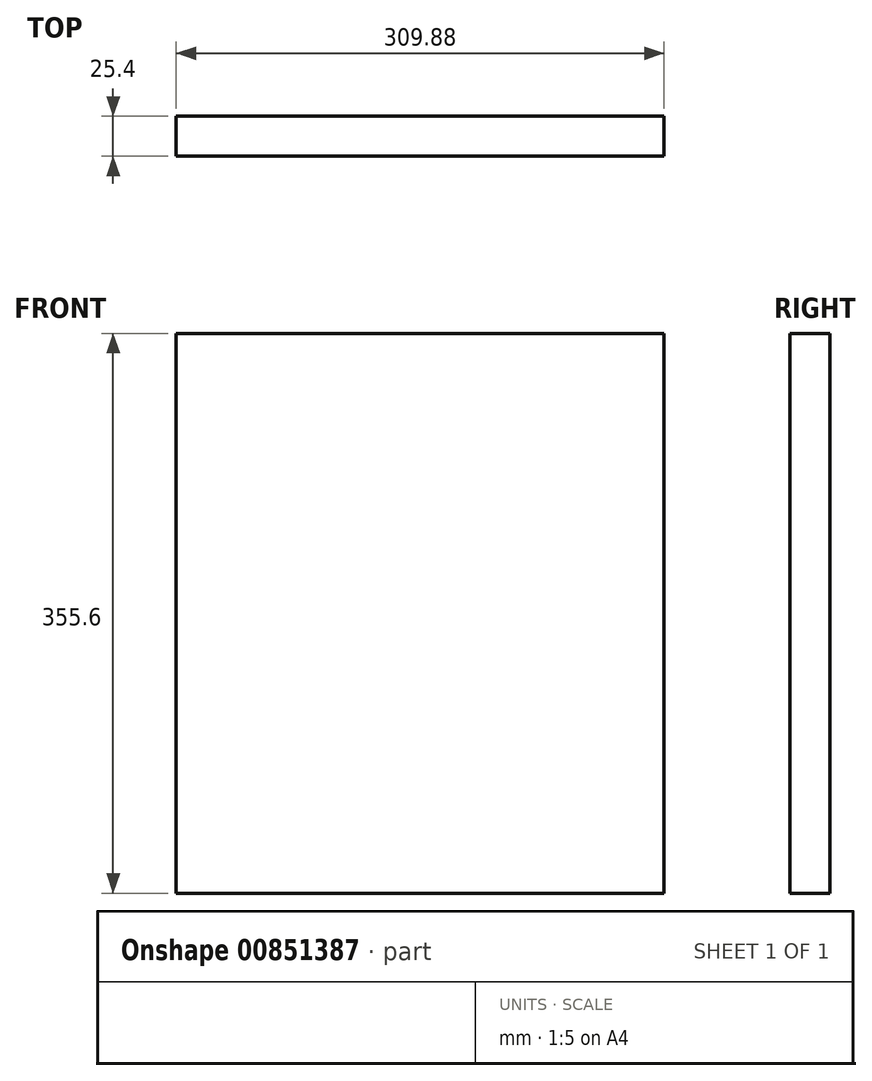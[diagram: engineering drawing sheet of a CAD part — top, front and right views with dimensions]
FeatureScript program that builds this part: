
annotation { "Feature Type Name" : "Feature", "Feature Type Description" : "" }
export const myFeature = defineFeature(function(context is Context, id is Id, definition is map)
    precondition{}
    {
        {
            var Q0;
            Q0=qCreatedBy(makeId("Front.planeOp"),FACE);
            var sketch = newSketch(context, id + "F0", { "sketchPlane" : qUnion([Q0])});
            skLineSegment(sketch, "E0.bottom", {"start": v(-58.11, 300.33) * mm, "end": v(251.77, 300.33) * mm});
            skLineSegment(sketch, "E0.top", {"start": v(-58.11, -55.27) * mm, "end": v(251.77, -55.27) * mm});
            skLineSegment(sketch, "E0.left", {"start": v(-58.11, 300.33) * mm, "end": v(-58.11, -55.27) * mm});
            skLineSegment(sketch, "E0.right", {"start": v(251.77, 300.33) * mm, "end": v(251.77, -55.27) * mm});
            skSolve(sketch);
        }
        {
            var Q0;
            Q0 = qSketchRegion(id + "F0", true);
            extrude(context, id + "F1", {"entities" : qUnion([Q0]), "depth" : 25.4 * mm, "offsetDistance" : 25.4 * mm});
        }
    });
